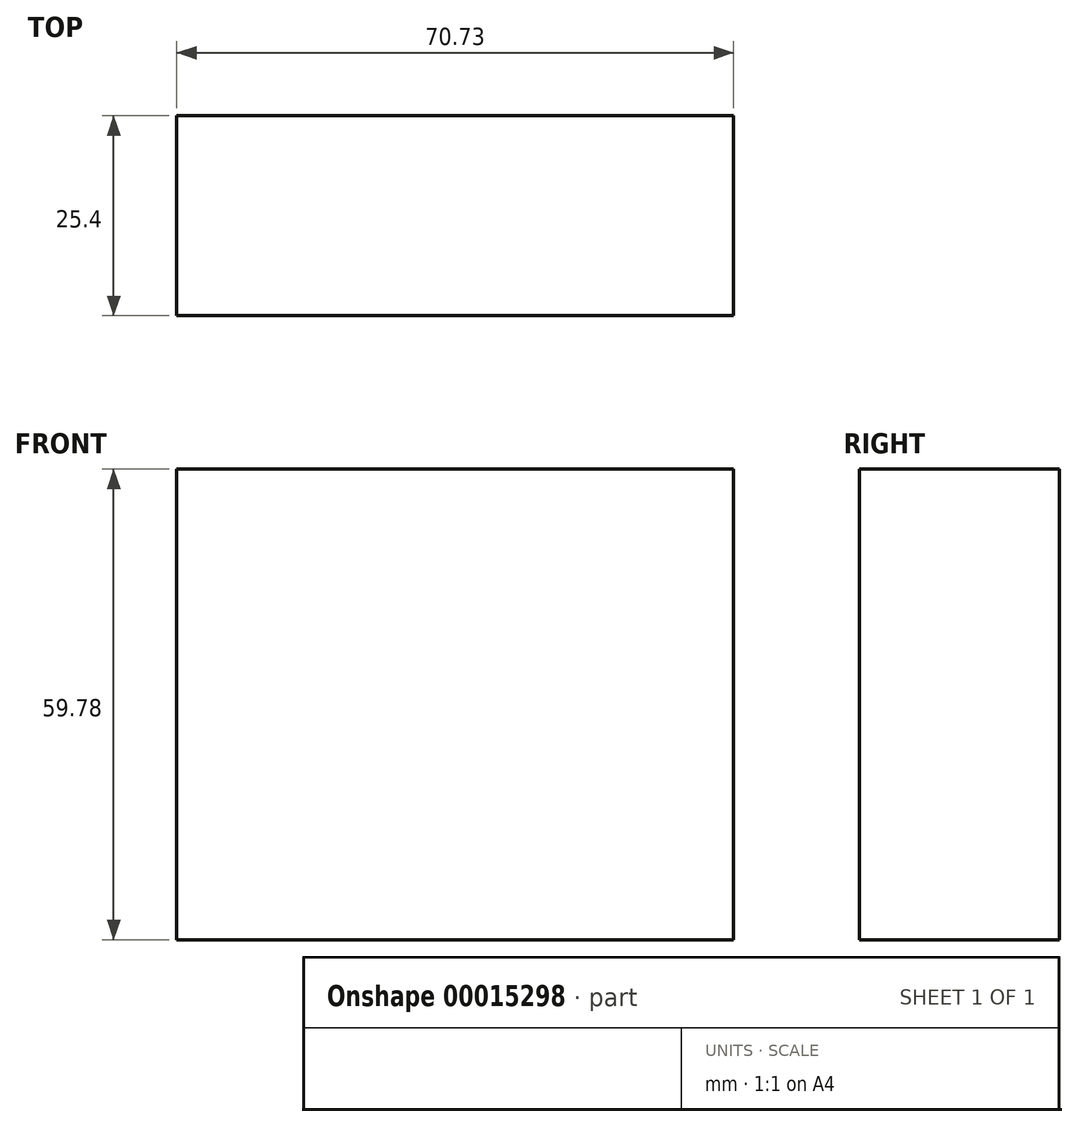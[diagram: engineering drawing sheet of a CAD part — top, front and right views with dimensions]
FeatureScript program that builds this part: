
annotation { "Feature Type Name" : "Feature", "Feature Type Description" : "" }
export const myFeature = defineFeature(function(context is Context, id is Id, definition is map)
    precondition{}
    {
        {
            var Q0;
            Q0=qCreatedBy(makeId("Front.planeOp"),FACE);
            var sketch = newSketch(context, id + "F0", { "sketchPlane" : qUnion([Q0])});
            skLineSegment(sketch, "E0.bottom", {"start": v(-39.43, 33.49) * mm, "end": v(31.3, 33.49) * mm});
            skLineSegment(sketch, "E0.top", {"start": v(-39.43, -26.29) * mm, "end": v(31.3, -26.29) * mm});
            skLineSegment(sketch, "E0.left", {"start": v(-39.43, 33.49) * mm, "end": v(-39.43, -26.29) * mm});
            skLineSegment(sketch, "E0.right", {"start": v(31.3, 33.49) * mm, "end": v(31.3, -26.29) * mm});
            skSolve(sketch);
        }
        {
            var Q0;
            Q0=makeQuery(id+"F0.imprint","IMPRINT",FACE,{"disambiguationData":[TD([[makeQuery(id+"F0.imprint","IMPRINT",EDGE,{"derivedFrom":sQuery(id+"F0.wireOp",EDGE,"E0.bottom")}),-1.0]])]});
            extrude(context, id + "F1", {"entities" : qUnion([Q0]), "depth" : 25.4 * mm});
        }
    });
